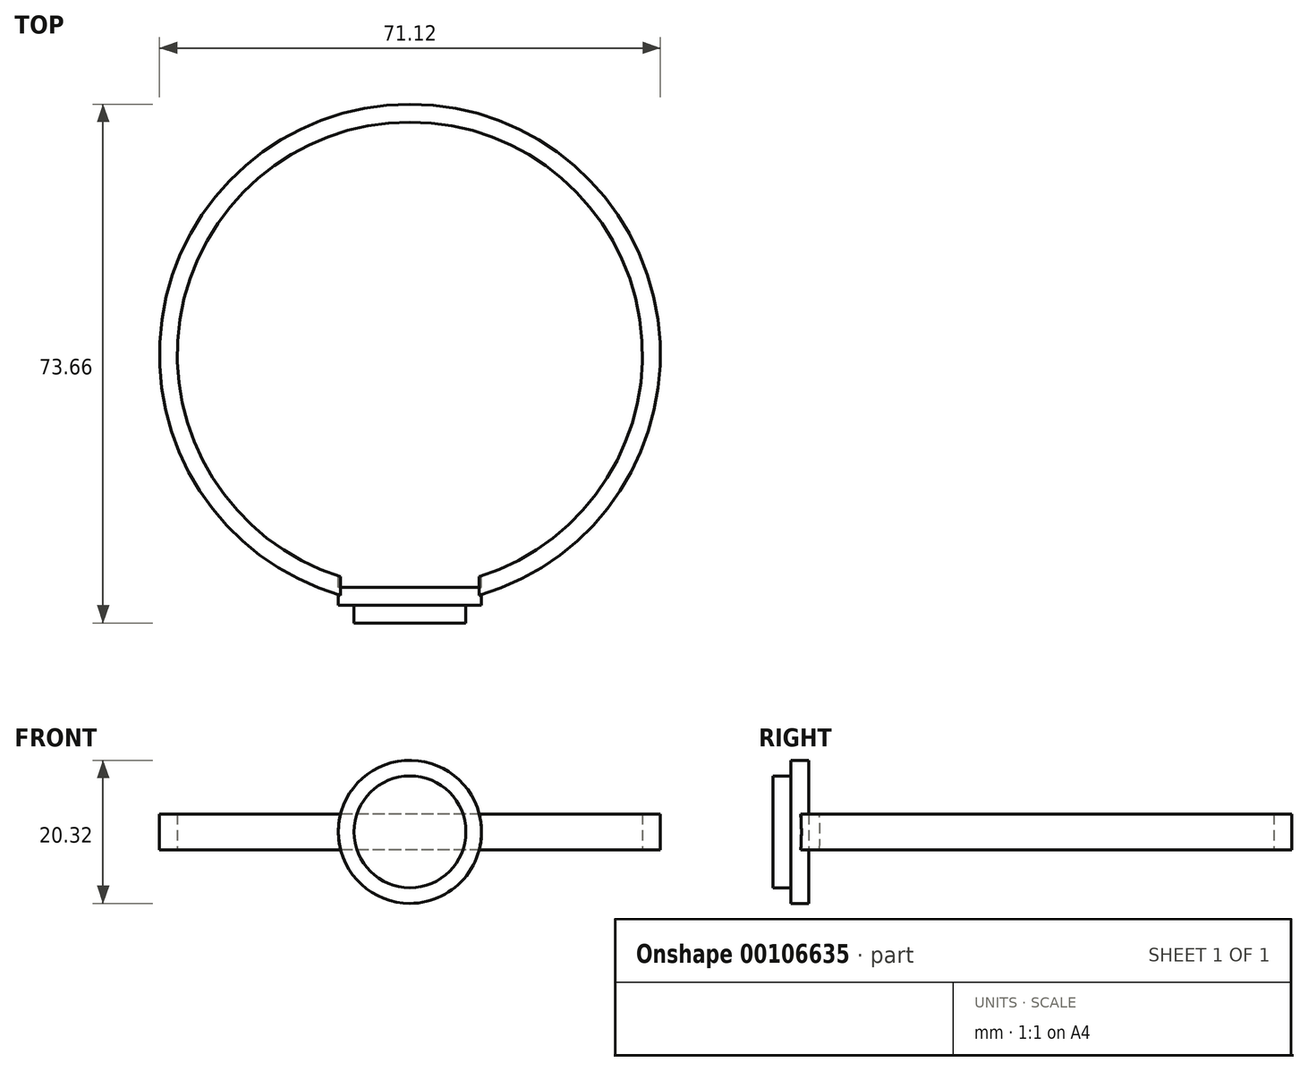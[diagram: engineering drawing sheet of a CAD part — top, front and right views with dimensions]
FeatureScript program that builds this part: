
annotation { "Feature Type Name" : "Feature", "Feature Type Description" : "" }
export const myFeature = defineFeature(function(context is Context, id is Id, definition is map)
    precondition{}
    {
        {
            var Q0;
            Q0=qCreatedBy(makeId("Top.planeOp"),FACE);
            var sketch = newSketch(context, id + "F0", { "sketchPlane" : qUnion([Q0])});
            skCircle(sketch, "E0", {"center": v(0, 0) * mm, "radius": 35.56 * mm});
            skCircle(sketch, "E1", {"center": v(0, 0) * mm, "radius": 33.02 * mm});
            skSolve(sketch);
        }
        {
            var Q0;
            Q0=makeQuery(id+"F0.imprint","IMPRINT",FACE,{"disambiguationData":[TD([[makeQuery(id+"F0.imprint","IMPRINT",EDGE,{"derivedFrom":sQuery(id+"F0.wireOp",EDGE,"E0")}),1.0]])]});
            extrude(context, id + "F1", {"entities" : qUnion([Q0]), "depth" : 2.54 * mm});
        }
        {
            var Q0;
            Q0 = qSketchRegion(id + "F0", true);
            extrude(context, id + "F2", {"entities" : qUnion([Q0]), "operationType" : NewBodyOperationType.ADD, "oppositeDirection" : true, "depth" : 2.54 * mm});
        }
        {
            var Q0;
            Q0=qCreatedBy(makeId("Front.planeOp"),FACE);
            var sketch = newSketch(context, id + "F3", { "sketchPlane" : qUnion([Q0])});
            skCircle(sketch, "E2", {"center": v(0, 0) * mm, "radius": 10.16 * mm});
            skSolve(sketch);
        }
        {
            var Q0;
            Q0=makeQuery(id+"F3.imprint","IMPRINT",FACE,{"disambiguationData":[TD([[makeQuery(id+"F3.imprint","IMPRINT",EDGE,{"derivedFrom":sQuery(id+"F3.wireOp",EDGE,"E2")}),1.0]])]});
            extrude(context, id + "F4", {"entities" : qUnion([Q0]), "operationType" : NewBodyOperationType.ADD, "depth" : 35.56 * mm});
        }
        {
            var Q0;
            Q0 = qSketchRegion(id + "F3", true);
            extrude(context, id + "F5", {"entities" : qUnion([Q0]), "operationType" : NewBodyOperationType.REMOVE, "depth" : 33.02 * mm});
        }
        {
            var Q0;
            Q0=makeQuery(id+"F4.opExtrude","CAP_FACE",FACE,{"disambiguationData":[OSD([sQuery(id+"F3.wireOp",EDGE,"E2")])],"isStart":false});
            var sketch = newSketch(context, id + "F6", { "sketchPlane" : qUnion([Q0])});
            skCircle(sketch, "E3", {"center": v(0, 0) * mm, "radius": 7.94 * mm});
            skSolve(sketch);
        }
        {
            var Q0;
            Q0 = qSketchRegion(id + "F6", true);
            extrude(context, id + "F7", {"entities" : qUnion([Q0]), "operationType" : NewBodyOperationType.ADD, "depth" : 2.54 * mm});
        }
    });
